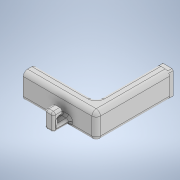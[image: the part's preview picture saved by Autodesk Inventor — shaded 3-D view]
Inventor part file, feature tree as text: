
AUTODESK INVENTOR PART (.ipt)
format: ipt  version: 2020 (Build 240168000, 168)  size: 269,312 bytes
history: native  units: in
note: dims shown in document units (in); Inventor stores cm internally (conversion verified against a paired STEP export)
features: sketch x6, extrude x4, hole x2, fillet x2
ambient origin geometry x8: Origin, YZ Plane, XZ Plane, XY Plane, X Axis, Y Axis, Z Axis, Center Point
bodies: Solid1 (feature_tree)
feature tree (14):
  extrude  "Extrusion1"  Depth=2.263in
  hole  "Hole1"  [1 undecoded]
  hole  "Hole2"  [1 undecoded]
  extrude  "Extrusion2"  Depth=0.125in
  fillet  "Fillet1"  Radius=0.1875in
  extrude  "Extrusion3"  Depth=0.0625in
  extrude  "Extrusion4"  Depth=0.0625in
  fillet  "Fillet2"  Radius=0.02in
  sketch  "Sketch1"  dims[d0=0.375in d1=2.263in]
  sketch  "Sketch2"  dims[d2=1.7475in d3=0.375in]
  sketch  "Sketch3"  dims[d4=0.75in d5=0.0in d6=0.1875in]
  sketch  "Sketch4"  dims[d7=0.125in d8=0.5in]
  sketch  "Sketch5"  dims[d9=0.089in d10=0.75in d11=0.225in d12=0.25in d13=0.5635in d14=0.5in d15=0.8108in d16=0.1875in]
  sketch  "Sketch6"  dims[d17=0.375in d18=0.185in d19=0.37in d20=0.0785in d21=0.75in d22=0.225in d23=0.25in d24=0.5635in d25=0.5in d26=0.8108in d27=0.02in d28=0.02in d29=0.02in d30=0.02in d31=0.13in d32=0.0in d33=0.125in d34=0.749in d35=0.125in d36=0.0in d37=0.25in d38=90.0deg d39=0.5in d40=0.0in d41=0.2in d42=135.0deg d43=0.5in d44=0.0in d45=0.0625in]
note: 2 required parameter values undecoded (feature->parameter linkage not recoverable at this tier; creation-order binding heuristic only, values carry confidence <= 0.55)
